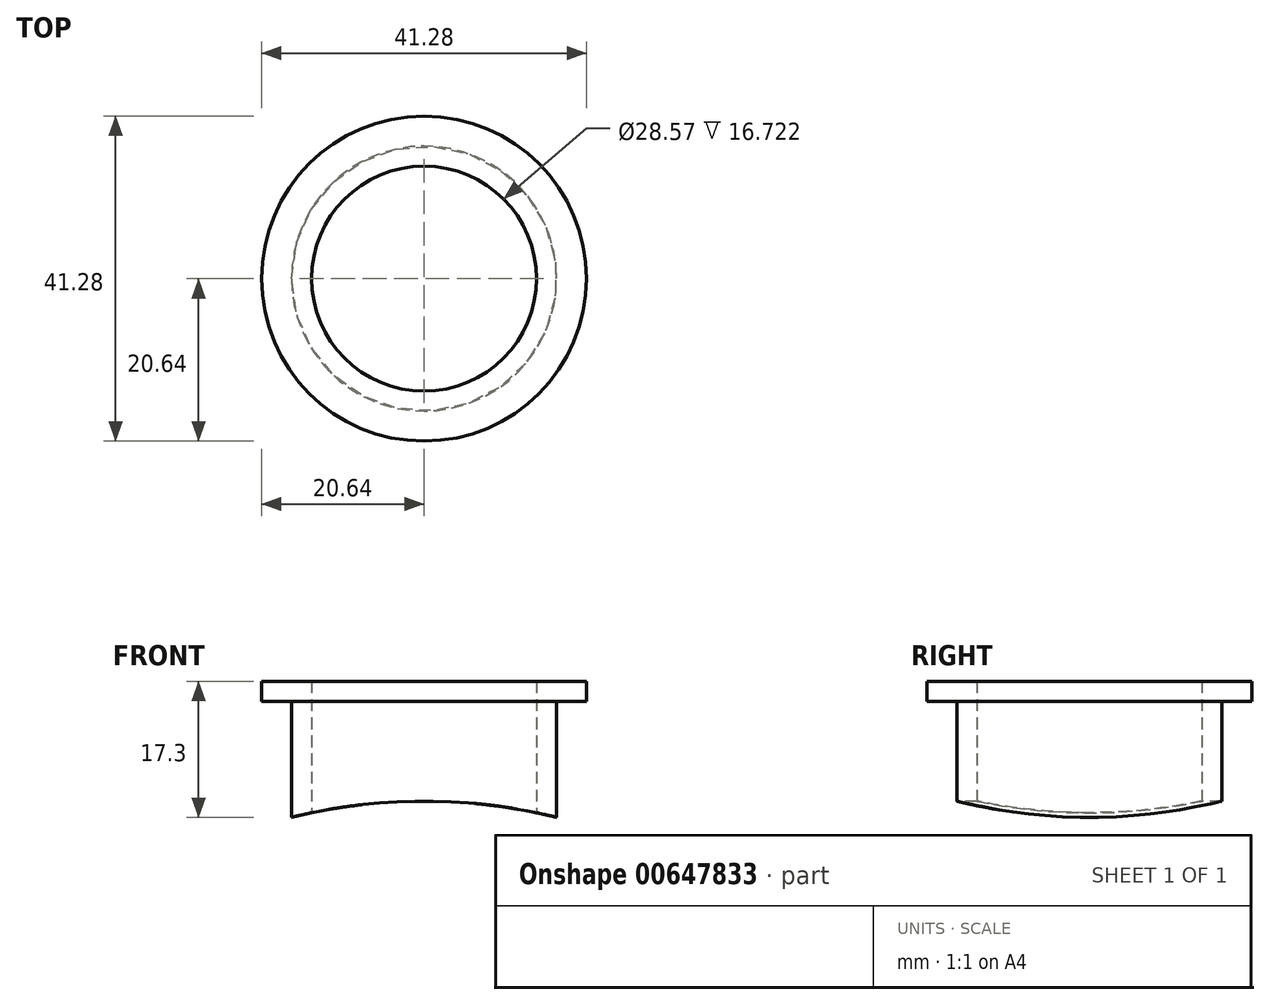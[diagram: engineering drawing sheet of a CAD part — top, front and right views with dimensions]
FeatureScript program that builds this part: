
annotation { "Feature Type Name" : "Feature", "Feature Type Description" : "" }
export const myFeature = defineFeature(function(context is Context, id is Id, definition is map)
    precondition{}
    {
        {
            var Q0;
            Q0=qCreatedBy(makeId("Front.planeOp"),FACE);
            var sketch = newSketch(context, id + "F0", { "sketchPlane" : qUnion([Q0])});
            skLineSegment(sketch, "E0", {"start": v(0, 0) * mm, "end": v(-14.29, 0) * mm, "construction": true});
            skLineSegment(sketch, "E1", {"start": v(-14.29, 0) * mm, "end": v(-16.83, 0) * mm});
            skLineSegment(sketch, "E2", {"start": v(-16.83, 0) * mm, "end": v(-16.83, 12.7) * mm});
            skLineSegment(sketch, "E3", {"start": v(-16.83, 12.7) * mm, "end": v(-14.29, 12.7) * mm});
            skLineSegment(sketch, "E4", {"start": v(-14.29, 12.7) * mm, "end": v(-14.29, 0) * mm});
            skLineSegment(sketch, "E5", {"start": v(0, 0) * mm, "end": v(0, 21.63) * mm, "construction": true});
            skLineSegment(sketch, "E6", {"start": v(-14.29, 12.7) * mm, "end": v(-14.29, 15.24) * mm});
            skLineSegment(sketch, "E7", {"start": v(-14.29, 15.24) * mm, "end": v(-20.64, 15.24) * mm});
            skLineSegment(sketch, "E8", {"start": v(-20.64, 15.24) * mm, "end": v(-20.64, 12.7) * mm});
            skLineSegment(sketch, "E9", {"start": v(-20.64, 12.7) * mm, "end": v(-16.83, 12.7) * mm});
            skSolve(sketch);
        }
        {
            var Q0;
            Q0 = qSketchRegion(id + "F0", true);
            var Q1;
            Q1=sQuery(id+"F0.wireOp",EDGE,"E5");
            revolve(context, id + "F1", {"entities" : qUnion([Q0]), "axis" : qUnion([Q1]), "revolveType" : RevolveType.FULL});
        }
        {
            var Q0;
            Q0=qCreatedBy(makeId("Front.planeOp"),FACE);
            var sketch = newSketch(context, id + "F2", { "sketchPlane" : qUnion([Q0])});
            skLineSegment(sketch, "E10", {"start": v(0, 0) * mm, "end": v(0, -69.85) * mm, "construction": true});
            skCircle(sketch, "E11", {"center": v(0, -69.85) * mm, "radius": 69.85 * mm});
            skSolve(sketch);
        }
        {
            var Q0;
            Q0=makeQuery(id+"F1.opRevolve","SWEPT_FACE",FACE,{"disambiguationData":[OSD([sQuery(id+"F0.wireOp",EDGE,"E1")])]});
            extrude(context, id + "F3", {"entities" : qUnion([Q0]), "operationType" : NewBodyOperationType.ADD, "depth" : 25.4 * mm, "offsetDistance" : 25.4 * mm});
        }
        {
            var Q0;
            Q0=makeQuery(id+"F2.imprint","IMPRINT",FACE,{"disambiguationData":[TD([[makeQuery(id+"F2.imprint","IMPRINT",EDGE,{"derivedFrom":sQuery(id+"F2.wireOp",EDGE,"E11")}),1.0]])]});
            extrude(context, id + "F4", {"entities" : qUnion([Q0]), "operationType" : NewBodyOperationType.REMOVE, "oppositeDirection" : true, "depth" : 25.4 * mm, "offsetDistance" : 25.4 * mm, "hasSecondDirection" : true, "secondDirectionOppositeDirection" : false, "secondDirectionDepth" : 25.4 * mm});
        }
    });
